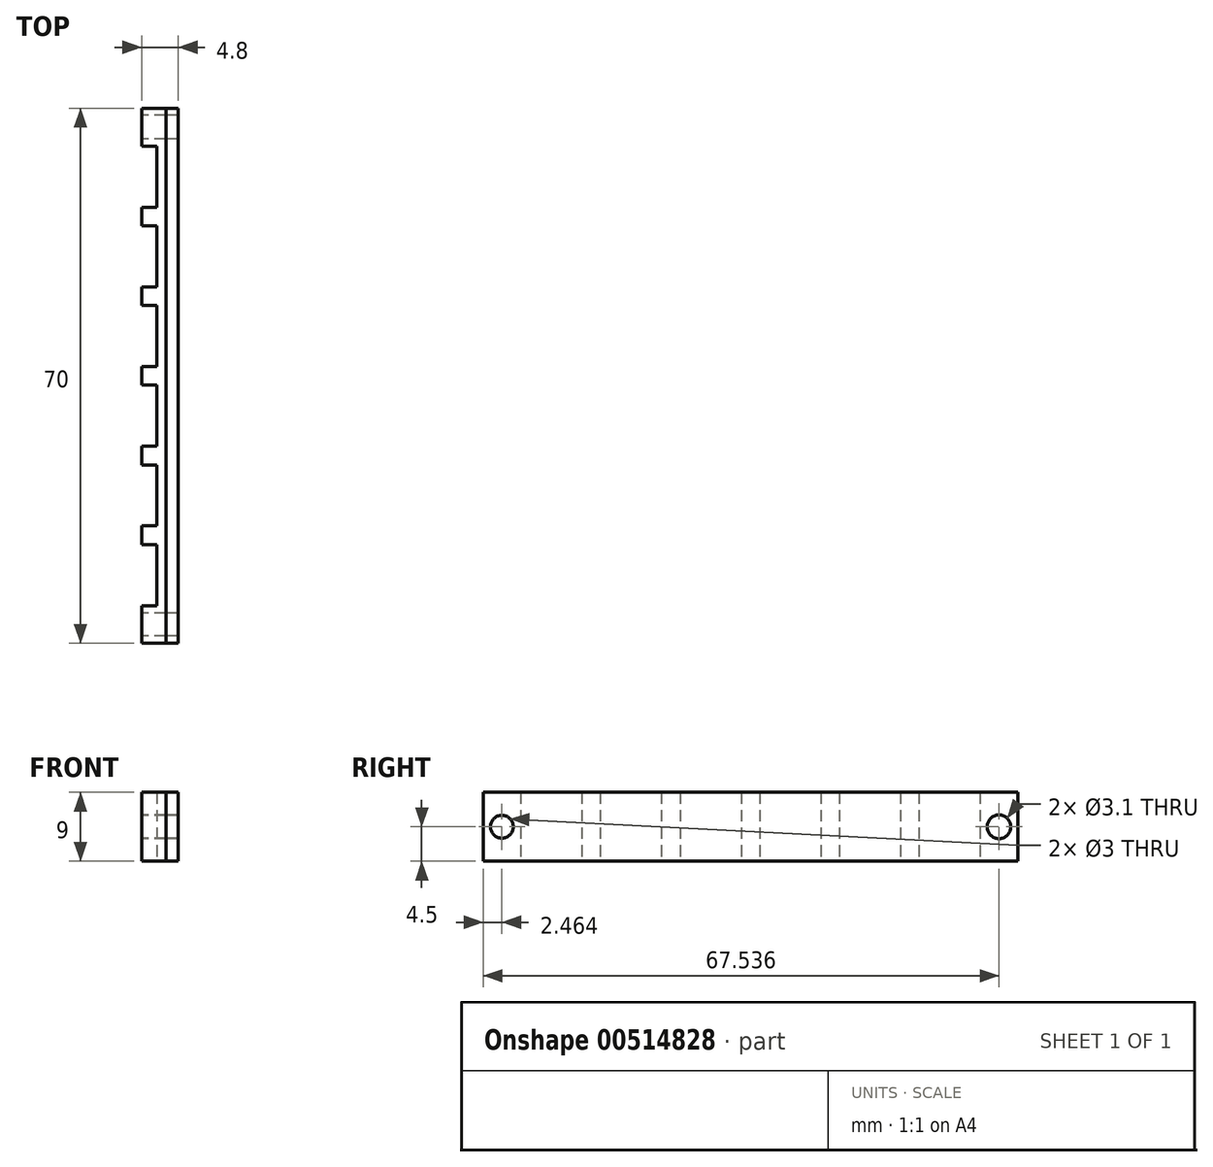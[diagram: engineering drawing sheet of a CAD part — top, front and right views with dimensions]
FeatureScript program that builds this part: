
annotation { "Feature Type Name" : "Feature", "Feature Type Description" : "" }
export const myFeature = defineFeature(function(context is Context, id is Id, definition is map)
    precondition{}
    {
        {
            var Q0;
            Q0=qCreatedBy(makeId("Top.planeOp"),FACE);
            var sketch = newSketch(context, id + "F0", { "sketchPlane" : qUnion([Q0])});
            skLineSegment(sketch, "E0.bottom", {"start": v(-1.2, 70) * mm, "end": v(0, 70) * mm});
            skLineSegment(sketch, "E0.top", {"start": v(-1.2, 0) * mm, "end": v(0, 0) * mm});
            skLineSegment(sketch, "E0.left", {"start": v(-1.2, 70) * mm, "end": v(-1.2, 0) * mm});
            skLineSegment(sketch, "E0.right", {"start": v(0, 70) * mm, "end": v(0, 0) * mm});
            skLineSegment(sketch, "E1.bottom", {"start": v(-1.2, 67.5) * mm, "end": v(-3.2, 67.5) * mm});
            skLineSegment(sketch, "E1.top", {"start": v(-1.2, 65.07) * mm, "end": v(-3.2, 65.07) * mm});
            skLineSegment(sketch, "E1.left", {"start": v(-1.2, 67.5) * mm, "end": v(-1.2, 65.07) * mm});
            skLineSegment(sketch, "E1.right", {"start": v(-3.2, 67.5) * mm, "end": v(-3.2, 65.07) * mm});
            skLineSegment(sketch, "E2.0.1.0", {"start": v(-3.2, 57.07) * mm, "end": v(-3.2, 54.64) * mm});
            skLineSegment(sketch, "E2.0.1.1", {"start": v(-1.2, 57.07) * mm, "end": v(-1.2, 54.64) * mm});
            skLineSegment(sketch, "E2.0.1.2", {"start": v(-1.2, 54.64) * mm, "end": v(-3.2, 54.64) * mm});
            skLineSegment(sketch, "E2.0.1.3", {"start": v(-1.2, 57.07) * mm, "end": v(-3.2, 57.07) * mm});
            skLineSegment(sketch, "E2.0.2.0", {"start": v(-3.2, 46.64) * mm, "end": v(-3.2, 44.21) * mm});
            skLineSegment(sketch, "E2.0.2.1", {"start": v(-1.2, 46.64) * mm, "end": v(-1.2, 44.21) * mm});
            skLineSegment(sketch, "E2.0.2.2", {"start": v(-1.2, 44.21) * mm, "end": v(-3.2, 44.21) * mm});
            skLineSegment(sketch, "E2.0.2.3", {"start": v(-1.2, 46.64) * mm, "end": v(-3.2, 46.64) * mm});
            skLineSegment(sketch, "E2.0.3.0", {"start": v(-3.2, 36.21) * mm, "end": v(-3.2, 33.79) * mm});
            skLineSegment(sketch, "E2.0.3.1", {"start": v(-1.2, 36.21) * mm, "end": v(-1.2, 33.79) * mm});
            skLineSegment(sketch, "E2.0.3.2", {"start": v(-1.2, 33.79) * mm, "end": v(-3.2, 33.79) * mm});
            skLineSegment(sketch, "E2.0.3.3", {"start": v(-1.2, 36.21) * mm, "end": v(-3.2, 36.21) * mm});
            skLineSegment(sketch, "E2.0.4.0", {"start": v(-3.2, 25.79) * mm, "end": v(-3.2, 23.36) * mm});
            skLineSegment(sketch, "E2.0.4.1", {"start": v(-1.2, 25.79) * mm, "end": v(-1.2, 23.36) * mm});
            skLineSegment(sketch, "E2.0.4.2", {"start": v(-1.2, 23.36) * mm, "end": v(-3.2, 23.36) * mm});
            skLineSegment(sketch, "E2.0.4.3", {"start": v(-1.2, 25.79) * mm, "end": v(-3.2, 25.79) * mm});
            skLineSegment(sketch, "E2.0.5.0", {"start": v(-3.2, 15.36) * mm, "end": v(-3.2, 12.93) * mm});
            skLineSegment(sketch, "E2.0.5.1", {"start": v(-1.2, 15.36) * mm, "end": v(-1.2, 12.93) * mm});
            skLineSegment(sketch, "E2.0.5.2", {"start": v(-1.2, 12.93) * mm, "end": v(-3.2, 12.93) * mm});
            skLineSegment(sketch, "E2.0.5.3", {"start": v(-1.2, 15.36) * mm, "end": v(-3.2, 15.36) * mm});
            skLineSegment(sketch, "E2.0.6.0", {"start": v(-3.2, 4.93) * mm, "end": v(-3.2, 2.5) * mm});
            skLineSegment(sketch, "E2.0.6.1", {"start": v(-1.2, 4.93) * mm, "end": v(-1.2, 2.5) * mm});
            skLineSegment(sketch, "E2.0.6.2", {"start": v(-1.2, 2.5) * mm, "end": v(-3.2, 2.5) * mm});
            skLineSegment(sketch, "E2.0.6.3", {"start": v(-1.2, 4.93) * mm, "end": v(-3.2, 4.93) * mm});
            skLineSegment(sketch, "E2.direction1", {"start": v(-3.2, 65.07) * mm, "end": v(0, 65.07) * mm, "construction": true});
            skLineSegment(sketch, "E2.direction2", {"start": v(-3.2, 65.07) * mm, "end": v(-3.2, 54.64) * mm, "construction": true});
            skLineSegment(sketch, "E3.bottom", {"start": v(-1.2, 70) * mm, "end": v(-3.2, 70) * mm});
            skLineSegment(sketch, "E3.left", {"start": v(-1.2, 70) * mm, "end": v(-1.2, 67.5) * mm});
            skLineSegment(sketch, "E3.right", {"start": v(-3.2, 70) * mm, "end": v(-3.2, 67.5) * mm});
            skLineSegment(sketch, "E4.bottom", {"start": v(-3.2, 2.5) * mm, "end": v(-1.2, 2.5) * mm});
            skLineSegment(sketch, "E4.top", {"start": v(-3.2, 0) * mm, "end": v(-1.2, 0) * mm});
            skLineSegment(sketch, "E4.left", {"start": v(-3.2, 2.5) * mm, "end": v(-3.2, 0) * mm});
            skLineSegment(sketch, "E4.right", {"start": v(-1.2, 2.5) * mm, "end": v(-1.2, 0) * mm});
            skSolve(sketch);
        }
        {
            var Q0;
            Q0=qCreatedBy(makeId("Top.planeOp"),FACE);
            var sketch = newSketch(context, id + "F1", { "sketchPlane" : qUnion([Q0])});
            skLineSegment(sketch, "E5.bottom", {"start": v(1.6, 70) * mm, "end": v(0, 70) * mm});
            skLineSegment(sketch, "E5.top", {"start": v(1.6, 0) * mm, "end": v(0, 0) * mm});
            skLineSegment(sketch, "E5.left", {"start": v(1.6, 70) * mm, "end": v(1.6, 0) * mm});
            skLineSegment(sketch, "E5.right", {"start": v(0, 70) * mm, "end": v(0, 0) * mm});
            skSolve(sketch);
        }
        {
            var Q0;
            Q0 = qSketchRegion(id + "F0", true);
            var Q1;
            Q1 = qSketchRegion(id + "F1", true);
            extrude(context, id + "F2", {"entities" : qUnion([Q0, Q1]), "depth" : 9 * mm, "offsetDistance" : 25 * mm});
        }
        {
            var Q0;
            Q0=makeQuery(id+"F2.opExtrude","SWEPT_FACE",FACE,{"disambiguationData":[OSD([sQuery(id+"F0.wireOp",EDGE,"E1.right"),sQuery(id+"F0.wireOp",EDGE,"E3.right")])]});
            var sketch = newSketch(context, id + "F3", { "sketchPlane" : qUnion([Q0])});
            skCircle(sketch, "E6", {"center": v(-67.54, 4.5) * mm, "radius": 1.55 * mm});
            skPoint(sketch, "E6.centerSnap0", {"position": v(-67.54, 9) * mm});
            skPoint(sketch, "E6.centerSnap1", {"position": v(-70, 4.5) * mm});
            skCircle(sketch, "E7", {"center": v(-2.46, 4.5) * mm, "radius": 1.5 * mm});
            skSolve(sketch);
        }
        {
            var Q0;
            Q0 = qSketchRegion(id + "F3", true);
            extrude(context, id + "F4", {"entities" : qUnion([Q0]), "operationType" : NewBodyOperationType.REMOVE, "endBound" : BoundingType.THROUGH_ALL, "oppositeDirection" : true, "depth" : 25 * mm, "offsetDistance" : 25 * mm});
        }
    });
